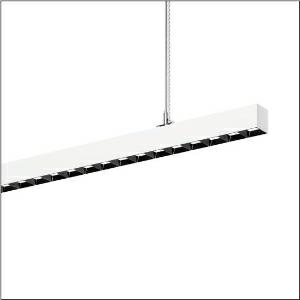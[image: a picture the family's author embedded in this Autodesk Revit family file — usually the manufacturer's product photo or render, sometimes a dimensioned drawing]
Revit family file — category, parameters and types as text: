
# Revit family: silica_r__21_51mx32tctdw_3fbf
name_source: partatom
category: Lighting Fixtures
units: mm (PartAtom-declared; Revit-internal decimal feet)

## family parameters
Cut with Voids When Loaded = No
Host = Face
Light Source = No
Part Type = Normal
Room Calculation Point = No
Round Connector Dimension = Use Diameter
Shared = No

## types (1)
- --- (1 x LED, 15540 lm, 133.6 W, 6500K)
    Apparent Load = 134 VA
    CIE Flux Codes = 84 99 100 60 100
    Color Rendering = 80
    Color Temperature = 6500K
    Default Elevation = 1800 mm
    Description = Silica® 21, office luminaire, primary light control with darklight reflector, of PMMA, black, CAT 2 (L<= 3000cd/m²), light emission: direct/indirect distribution, primary light characteristic: symmetric, installation type: suspended mounting, LED, rated luminous flux: 15.540lm, luminous efficacy: 111lm/W, light colour: 8tw, colour temperature: 2700..6500K, control gear: DALI DT8, with terminal, 3+2-pole, max. 2.5mm², mains connection: 220..240V, AC, 50/60Hz, rated input power: 140.3W, luminaire housing, of aluminium, traffic white (RAL 9016), length: 3.004mm, width: 53mm, height: 53mm, protection rating (complete): IP20, insulation class (complete): insulation class I (protective earthing), certification: CE, permissible operating ambient temperature: 0..+35°C, standard: EN 50419, packaging unit: 1 piece
    Height = 53 mm
    Lamp = 1 x LED
    Lamp Light Flux = 15540 lm
    Lamp Power = 133.6 W
    Lamp count = 1
    Length = 3004 mm
    Luminous efficacy = 116 lm/W
    Manufacturer = Siteco
    ModVariant = No
    Model = 51MX32TCTDW
    Mounting Place = Ceiling
    Mounting Type = Pendant
    Number of Poles = 1
    OnlyDefault = Yes
    Power Factor = 1
    Product Name = Silica® 21
    Product group = office luminaire | ceiling pendant
    ProductGroupID = 904
    Protection Class = Protection class I
    Protection Degree = IP 20
    RLX_Detail_Level = 1
    RLX_Emergency_Light_Flux = 0 lm
    RLX_Emergency_Type = 0
    RLX_Emergency_Type_DB = No
    RlxData = <blob elided: 61001 chars, md5=caae1972>
    Socket = socket
    Standby Power = 0 W
    System Light Flux = 15540 lm
    System Power = 134 W
    Type Comments = individual setting
    Type Image = l_1335871.jpg
    URL = http://relux.com
    VarID = @adj_139950
    Voltage = 0 V
    Weight = 0.00 kg
    Width = 53 mm

## geometry (parser evidence)
native form markers: Blend x4, Sweep x14
no freeform markers — native parametric forms only
